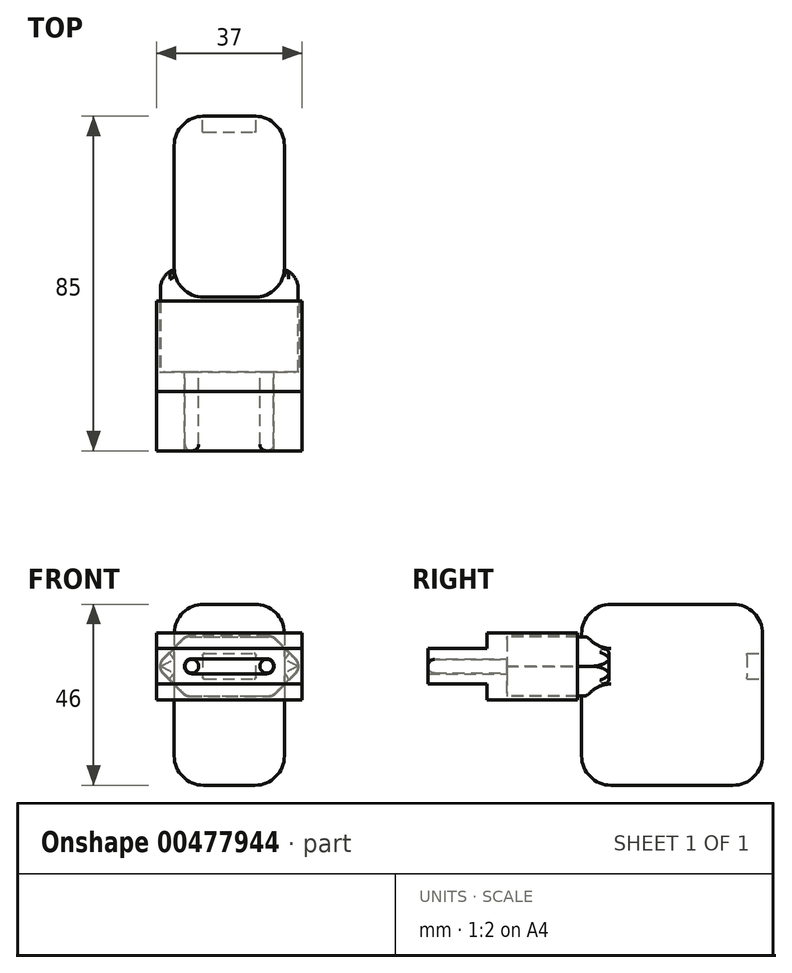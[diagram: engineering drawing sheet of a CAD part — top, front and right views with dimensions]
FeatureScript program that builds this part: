
annotation { "Feature Type Name" : "Feature", "Feature Type Description" : "" }
export const myFeature = defineFeature(function(context is Context, id is Id, definition is map)
    precondition{}
    {
        {
            var Q0;
            Q0=qCreatedBy(makeId("Front.planeOp"),FACE);
            var sketch = newSketch(context, id + "F0", { "sketchPlane" : qUnion([Q0])});
            skLineSegment(sketch, "E0.bottom", {"start": v(-14, 23) * mm, "end": v(14, 23) * mm});
            skLineSegment(sketch, "E0.top", {"start": v(-14, -23) * mm, "end": v(14, -23) * mm});
            skLineSegment(sketch, "E0.left", {"start": v(-14, 23) * mm, "end": v(-14, -23) * mm});
            skLineSegment(sketch, "E0.right", {"start": v(14, 23) * mm, "end": v(14, -23) * mm});
            skPoint(sketch, "E0.middle", {"position": v(0, 0) * mm});
            skLineSegment(sketch, "E1.bottom", {"start": v(-6.75, 10.5) * mm, "end": v(6.75, 10.5) * mm});
            skLineSegment(sketch, "E1.top", {"start": v(-6.75, 4) * mm, "end": v(6.75, 4) * mm});
            skLineSegment(sketch, "E1.left", {"start": v(-6.75, 10.5) * mm, "end": v(-6.75, 4) * mm});
            skLineSegment(sketch, "E1.right", {"start": v(6.75, 10.5) * mm, "end": v(6.75, 4) * mm});
            skPoint(sketch, "E1.middle", {"position": v(0, 7.25) * mm});
            skLineSegment(sketch, "E2.bottom", {"start": v(-17.5, 14.75) * mm, "end": v(17.5, 14.75) * mm});
            skLineSegment(sketch, "E2.top", {"start": v(-17.5, -0.25) * mm, "end": v(17.5, -0.25) * mm});
            skLineSegment(sketch, "E2.left", {"start": v(-17.5, 14.75) * mm, "end": v(-17.5, -0.25) * mm});
            skLineSegment(sketch, "E2.right", {"start": v(17.5, 14.75) * mm, "end": v(17.5, -0.25) * mm});
            skCircle(sketch, "E3", {"center": v(-9.5, 7.25) * mm, "radius": 1.75 * mm});
            skCircle(sketch, "E4", {"center": v(9.5, 7.25) * mm, "radius": 1.75 * mm});
            skSolve(sketch);
        }
        {
            var Q0;
            {var subQ0=sQuery(id+"F0.wireOp",EDGE,"E0.top");Q0=makeQuery(id+"F0.imprint","IMPRINT",FACE,{"disambiguationData":[TD([[makeQuery(id+"F0.imprint","IMPRINT",EDGE,{"derivedFrom":subQ0}),1.0]])]});}
            var Q1;
            Q1=makeQuery(id+"F0.imprint","IMPRINT",FACE,{"disambiguationData":[TD([[makeQuery(id+"F0.imprint","IMPRINT",EDGE,{"derivedFrom":sQuery(id+"F0.wireOp",EDGE,"E1.bottom")}),1.0]])]});
            var Q2;
            {var subQ0=sQuery(id+"F0.wireOp",EDGE,"E0.bottom");Q2=makeQuery(id+"F0.imprint","IMPRINT",FACE,{"disambiguationData":[TD([[makeQuery(id+"F0.imprint","IMPRINT",EDGE,{"derivedFrom":subQ0}),-1.0]])]});}
            var Q3;
            Q3=makeQuery(id+"F0.imprint","IMPRINT",FACE,{"disambiguationData":[TD([[makeQuery(id+"F0.imprint","IMPRINT",EDGE,{"derivedFrom":sQuery(id+"F0.wireOp",EDGE,"E1.bottom")}),-1.0]])]});
            var Q4;
            Q4=makeQuery(id+"F0.imprint","IMPRINT",FACE,{"disambiguationData":[TD([[makeQuery(id+"F0.imprint","IMPRINT",EDGE,{"derivedFrom":sQuery(id+"F0.wireOp",EDGE,"E3")}),1.0]])]});
            var Q5;
            Q5=makeQuery(id+"F0.imprint","IMPRINT",FACE,{"disambiguationData":[TD([[makeQuery(id+"F0.imprint","IMPRINT",EDGE,{"derivedFrom":sQuery(id+"F0.wireOp",EDGE,"E4")}),1.0]])]});
            extrude(context, id + "F1", {"entities" : qUnion([Q0, Q1, Q2, Q3, Q4, Q5]), "depth" : 46 * mm, "offsetDistance" : 25 * mm});
        }
        {
            var Q0;
            Q0=makeQuery(id+"F1.opExtrude","CAP_FACE",FACE,{"disambiguationData":[OSD([sQuery(id+"F0.wireOp",EDGE,"E0.bottom"),sQuery(id+"F0.wireOp",EDGE,"E0.top"),sQuery(id+"F0.wireOp",EDGE,"E0.left"),sQuery(id+"F0.wireOp",EDGE,"E0.right")])],"isStart":false});
            var sketch = newSketch(context, id + "F2", { "sketchPlane" : qUnion([Q0])});
            skLineSegment(sketch, "E5.0", {"start": v(-17.5, 14.75) * mm, "end": v(17.5, 14.75) * mm});
            skLineSegment(sketch, "E6.0", {"start": v(-17.5, 14.75) * mm, "end": v(-17.5, -0.25) * mm});
            skLineSegment(sketch, "E7.0", {"start": v(-17.5, -0.25) * mm, "end": v(17.5, -0.25) * mm});
            skLineSegment(sketch, "E8.0", {"start": v(17.5, 14.75) * mm, "end": v(17.5, -0.25) * mm});
            skPoint(sketch, "E9.0", {"position": v(0, 7.25) * mm});
            skCircle(sketch, "E10.0", {"center": v(-9.5, 7.25) * mm, "radius": 1.75 * mm});
            skCircle(sketch, "E10.1", {"center": v(9.5, 7.25) * mm, "radius": 1.75 * mm});
            skSolve(sketch);
        }
        {
            var Q0;
            Q0=makeQuery(id+"F2.imprint","IMPRINT",FACE,{"disambiguationData":[TD([[makeQuery(id+"F2.imprint","IMPRINT",EDGE,{"derivedFrom":sQuery(id+"F2.wireOp",EDGE,"E10.0")}),1.0]])]});
            var Q1;
            Q1=makeQuery(id+"F2.imprint","IMPRINT",FACE,{"disambiguationData":[TD([[makeQuery(id+"F2.imprint","IMPRINT",EDGE,{"derivedFrom":sQuery(id+"F2.wireOp",EDGE,"E10.1")}),1.0]])]});
            extrude(context, id + "F3", {"entities" : qUnion([Q0, Q1]), "operationType" : NewBodyOperationType.ADD, "depth" : 39 * mm, "offsetDistance" : 25 * mm});
        }
        {
            var Q0;
            {var subQ0=sQuery(id+"F2.wireOp",EDGE,"E6.0");Q0=makeQuery(id+"F2.imprint","IMPRINT",FACE,{"disambiguationData":[TD([[makeQuery(id+"F2.imprint","IMPRINT",EDGE,{"derivedFrom":subQ0}),1.0]])]});}
            var Q1;
            Q1=makeQuery(id+"F2.imprint","IMPRINT",FACE,{"disambiguationData":[TD([[makeQuery(id+"F2.imprint","IMPRINT",EDGE,{"derivedFrom":sQuery(id+"F2.wireOp",EDGE,"E10.0")}),-1.0]])]});
            var Q2;
            {var subQ0=sQuery(id+"F2.wireOp",EDGE,"E8.0");Q2=makeQuery(id+"F2.imprint","IMPRINT",FACE,{"disambiguationData":[TD([[makeQuery(id+"F2.imprint","IMPRINT",EDGE,{"derivedFrom":subQ0}),-1.0]])]});}
            extrude(context, id + "F4", {"entities" : qUnion([Q0, Q1, Q2]), "operationType" : NewBodyOperationType.ADD, "depth" : 19 * mm, "offsetDistance" : 25 * mm});
        }
        {
            var Q0;
            {var subQ0=sQuery(id+"F2.wireOp",EDGE,"E6.0");Q0=makeQuery(id+"F2.imprint","IMPRINT",FACE,{"disambiguationData":[TD([[makeQuery(id+"F2.imprint","IMPRINT",EDGE,{"derivedFrom":subQ0}),1.0]])]});}
            var Q1;
            {var subQ0=sQuery(id+"F2.wireOp",EDGE,"E8.0");Q1=makeQuery(id+"F2.imprint","IMPRINT",FACE,{"disambiguationData":[TD([[makeQuery(id+"F2.imprint","IMPRINT",EDGE,{"derivedFrom":subQ0}),-1.0]])]});}
            extrude(context, id + "F5", {"entities" : qUnion([Q0, Q1]), "operationType" : NewBodyOperationType.ADD, "oppositeDirection" : true, "depth" : 7 * mm, "offsetDistance" : 25 * mm});
        }
        {
            var Q0;
            Q0=makeQuery(id+"F3.opExtrude","CAP_EDGE",EDGE,{"disambiguationData":[OSD([sQuery(id+"F2.wireOp",EDGE,"E10.0")])],"isStart":false});
            var Q1;
            Q1=makeQuery(id+"F3.opExtrude","CAP_EDGE",EDGE,{"disambiguationData":[OSD([sQuery(id+"F2.wireOp",EDGE,"E10.1")])],"isStart":false});
            fillet(context, id + "F6", {"entities" : qUnion([Q0, Q1]), "radius" : 1.65 * mm, "tangentPropagation" : true, "allowEdgeOverflow" : false});
        }
        {
            var Q0;
            Q0=makeQuery(id+"F5.opExtrude","CAP_EDGE",EDGE,{"disambiguationData":[OSD([sQuery(id+"F2.wireOp",EDGE,"E8.0")])],"isStart":false});
            var Q1;
            Q1=makeQuery(id+"F5.opExtrude","CAP_EDGE",EDGE,{"disambiguationData":[OSD([sQuery(id+"F2.wireOp",EDGE,"E6.0")])],"isStart":false});
            var Q2;
            {var subQ0=sQuery(id+"F2.wireOp",EDGE,"E7.0");Q2=makeQuery(id+"F5.opExtrude","CAP_EDGE",EDGE,{"disambiguationData":[OSD([subQ0]),TDD([makeQuery(id+"F2.imprint","IMPRINT",EDGE,{"disambiguationData":[TD([[makeQuery(id+"F2.imprint","INTERSECT",VERTEX,{"derivedFrom":[subQ0,sQuery(id+"F2.wireOp",EDGE,"E8.0")]}),1.0]])],"derivedFrom":subQ0})])],"isStart":false});}
            var Q3;
            {var subQ0=sQuery(id+"F2.wireOp",EDGE,"E5.0");Q3=makeQuery(id+"F5.opExtrude","CAP_EDGE",EDGE,{"disambiguationData":[OSD([subQ0]),TDD([makeQuery(id+"F2.imprint","IMPRINT",EDGE,{"disambiguationData":[TD([[makeQuery(id+"F2.imprint","INTERSECT",VERTEX,{"derivedFrom":[subQ0,sQuery(id+"F2.wireOp",EDGE,"E8.0")]}),1.0]])],"derivedFrom":subQ0})])],"isStart":false});}
            var Q4;
            {var subQ0=sQuery(id+"F2.wireOp",EDGE,"E7.0");Q4=makeQuery(id+"F5.opExtrude","CAP_EDGE",EDGE,{"disambiguationData":[OSD([subQ0]),TDD([makeQuery(id+"F2.imprint","IMPRINT",EDGE,{"disambiguationData":[TD([[makeQuery(id+"F2.imprint","INTERSECT",VERTEX,{"derivedFrom":[sQuery(id+"F2.wireOp",EDGE,"E6.0"),subQ0]}),-1.0]])],"derivedFrom":subQ0})])],"isStart":false});}
            var Q5;
            {var subQ0=sQuery(id+"F2.wireOp",EDGE,"E5.0");Q5=makeQuery(id+"F5.opExtrude","CAP_EDGE",EDGE,{"disambiguationData":[OSD([subQ0]),TDD([makeQuery(id+"F2.imprint","IMPRINT",EDGE,{"disambiguationData":[TD([[makeQuery(id+"F2.imprint","INTERSECT",VERTEX,{"derivedFrom":[subQ0,sQuery(id+"F2.wireOp",EDGE,"E6.0")]}),-1.0]])],"derivedFrom":subQ0})])],"isStart":false});}
            fillet(context, id + "F7", {"entities" : qUnion([Q0, Q1, Q2, Q3, Q4, Q5]), "radius" : 5 * mm, "tangentPropagation" : true, "allowEdgeOverflow" : false});
        }
        {
            var Q0;
            {var subQ0=sQuery(id+"F2.wireOp",EDGE,"E8.0");var subQ1=sQuery(id+"F2.wireOp",EDGE,"E5.0");Q0=makeQuery(id+"F5.boolean.opBoolean","MERGE",EDGE,{"derivedFrom":[makeQuery(id+"F4.opExtrude","SWEPT_EDGE",EDGE,{"disambiguationData":[OSD([subQ1,subQ0])]}),makeQuery(id+"F5.opExtrude","SWEPT_EDGE",EDGE,{"disambiguationData":[OSD([subQ1,subQ0])]})]});}
            var Q1;
            {var subQ0=sQuery(id+"F2.wireOp",EDGE,"E8.0");var subQ1=sQuery(id+"F2.wireOp",EDGE,"E7.0");Q1=makeQuery(id+"F5.boolean.opBoolean","MERGE",EDGE,{"derivedFrom":[makeQuery(id+"F4.opExtrude","SWEPT_EDGE",EDGE,{"disambiguationData":[OSD([subQ1,subQ0])]}),makeQuery(id+"F5.opExtrude","SWEPT_EDGE",EDGE,{"disambiguationData":[OSD([subQ1,subQ0])]})]});}
            var Q2;
            {var subQ0=sQuery(id+"F2.wireOp",EDGE,"E7.0");var subQ1=sQuery(id+"F2.wireOp",EDGE,"E6.0");Q2=makeQuery(id+"F5.boolean.opBoolean","MERGE",EDGE,{"derivedFrom":[makeQuery(id+"F4.opExtrude","SWEPT_EDGE",EDGE,{"disambiguationData":[OSD([subQ1,subQ0])]}),makeQuery(id+"F5.opExtrude","SWEPT_EDGE",EDGE,{"disambiguationData":[OSD([subQ1,subQ0])]})]});}
            var Q3;
            {var subQ0=sQuery(id+"F2.wireOp",EDGE,"E6.0");var subQ1=sQuery(id+"F2.wireOp",EDGE,"E5.0");Q3=makeQuery(id+"F5.boolean.opBoolean","MERGE",EDGE,{"derivedFrom":[makeQuery(id+"F4.opExtrude","SWEPT_EDGE",EDGE,{"disambiguationData":[OSD([subQ1,subQ0])]}),makeQuery(id+"F5.opExtrude","SWEPT_EDGE",EDGE,{"disambiguationData":[OSD([subQ1,subQ0])]})]});}
            chamfer(context, id + "F8", {"entities" : qUnion([Q0, Q1, Q2, Q3]), "width" : 6.5 * mm});
        }
        {
            var Q0;
            {var subQ0=sQuery(id+"F2.wireOp",EDGE,"E8.0");var subQ1=sQuery(id+"F2.wireOp",EDGE,"E7.0");Q0=makeQuery(id+"F8.opChamfer","BLEND_EDGE",EDGE,{"blendedFrom":[makeQuery(id+"F5.boolean.opBoolean","MERGE",EDGE,{"derivedFrom":[makeQuery(id+"F4.opExtrude","SWEPT_EDGE",EDGE,{"disambiguationData":[OSD([subQ1,subQ0])]}),makeQuery(id+"F5.opExtrude","SWEPT_EDGE",EDGE,{"disambiguationData":[OSD([subQ1,subQ0])]})]}),makeQuery(id+"F5.boolean.opBoolean","MERGE",FACE,{"derivedFrom":[makeQuery(id+"F4.opExtrude","SWEPT_FACE",FACE,{"disambiguationData":[OSD([subQ1])]}),makeQuery(id+"F5.opExtrude","SWEPT_FACE",FACE,{"disambiguationData":[OSD([subQ1]),TDD([makeQuery(id+"F2.imprint","IMPRINT",EDGE,{"disambiguationData":[TD([[makeQuery(id+"F2.imprint","INTERSECT",VERTEX,{"derivedFrom":[sQuery(id+"F2.wireOp",EDGE,"E6.0"),subQ1]}),-1.0]])],"derivedFrom":subQ1})])]}),makeQuery(id+"F5.opExtrude","SWEPT_FACE",FACE,{"disambiguationData":[OSD([subQ1]),TDD([makeQuery(id+"F2.imprint","IMPRINT",EDGE,{"disambiguationData":[TD([[makeQuery(id+"F2.imprint","INTERSECT",VERTEX,{"derivedFrom":[subQ1,subQ0]}),1.0]])],"derivedFrom":subQ1})])]})]})],"blendedInto":[makeQuery(id+"F5.boolean.opBoolean","MERGE",FACE,{"derivedFrom":[makeQuery(id+"F4.opExtrude","SWEPT_FACE",FACE,{"disambiguationData":[OSD([subQ1])]}),makeQuery(id+"F5.opExtrude","SWEPT_FACE",FACE,{"disambiguationData":[OSD([subQ1]),TDD([makeQuery(id+"F2.imprint","IMPRINT",EDGE,{"disambiguationData":[TD([[makeQuery(id+"F2.imprint","INTERSECT",VERTEX,{"derivedFrom":[sQuery(id+"F2.wireOp",EDGE,"E6.0"),subQ1]}),-1.0]])],"derivedFrom":subQ1})])]}),makeQuery(id+"F5.opExtrude","SWEPT_FACE",FACE,{"disambiguationData":[OSD([subQ1]),TDD([makeQuery(id+"F2.imprint","IMPRINT",EDGE,{"disambiguationData":[TD([[makeQuery(id+"F2.imprint","INTERSECT",VERTEX,{"derivedFrom":[subQ1,subQ0]}),1.0]])],"derivedFrom":subQ1})])]})]})]});}
            var Q1;
            {var subQ0=sQuery(id+"F2.wireOp",EDGE,"E7.0");var subQ1=sQuery(id+"F2.wireOp",EDGE,"E6.0");Q1=makeQuery(id+"F8.opChamfer","BLEND_EDGE",EDGE,{"blendedFrom":[makeQuery(id+"F5.boolean.opBoolean","MERGE",EDGE,{"derivedFrom":[makeQuery(id+"F4.opExtrude","SWEPT_EDGE",EDGE,{"disambiguationData":[OSD([subQ1,subQ0])]}),makeQuery(id+"F5.opExtrude","SWEPT_EDGE",EDGE,{"disambiguationData":[OSD([subQ1,subQ0])]})]}),makeQuery(id+"F5.boolean.opBoolean","MERGE",FACE,{"derivedFrom":[makeQuery(id+"F4.opExtrude","SWEPT_FACE",FACE,{"disambiguationData":[OSD([subQ0])]}),makeQuery(id+"F5.opExtrude","SWEPT_FACE",FACE,{"disambiguationData":[OSD([subQ0]),TDD([makeQuery(id+"F2.imprint","IMPRINT",EDGE,{"disambiguationData":[TD([[makeQuery(id+"F2.imprint","INTERSECT",VERTEX,{"derivedFrom":[subQ1,subQ0]}),-1.0]])],"derivedFrom":subQ0})])]}),makeQuery(id+"F5.opExtrude","SWEPT_FACE",FACE,{"disambiguationData":[OSD([subQ0]),TDD([makeQuery(id+"F2.imprint","IMPRINT",EDGE,{"disambiguationData":[TD([[makeQuery(id+"F2.imprint","INTERSECT",VERTEX,{"derivedFrom":[subQ0,sQuery(id+"F2.wireOp",EDGE,"E8.0")]}),1.0]])],"derivedFrom":subQ0})])]})]})],"blendedInto":[makeQuery(id+"F5.boolean.opBoolean","MERGE",FACE,{"derivedFrom":[makeQuery(id+"F4.opExtrude","SWEPT_FACE",FACE,{"disambiguationData":[OSD([subQ0])]}),makeQuery(id+"F5.opExtrude","SWEPT_FACE",FACE,{"disambiguationData":[OSD([subQ0]),TDD([makeQuery(id+"F2.imprint","IMPRINT",EDGE,{"disambiguationData":[TD([[makeQuery(id+"F2.imprint","INTERSECT",VERTEX,{"derivedFrom":[subQ1,subQ0]}),-1.0]])],"derivedFrom":subQ0})])]}),makeQuery(id+"F5.opExtrude","SWEPT_FACE",FACE,{"disambiguationData":[OSD([subQ0]),TDD([makeQuery(id+"F2.imprint","IMPRINT",EDGE,{"disambiguationData":[TD([[makeQuery(id+"F2.imprint","INTERSECT",VERTEX,{"derivedFrom":[subQ0,sQuery(id+"F2.wireOp",EDGE,"E8.0")]}),1.0]])],"derivedFrom":subQ0})])]})]})]});}
            var Q2;
            {var subQ0=sQuery(id+"F2.wireOp",EDGE,"E6.0");var subQ1=sQuery(id+"F2.wireOp",EDGE,"E7.0");Q2=makeQuery(id+"F8.opChamfer","BLEND_EDGE",EDGE,{"blendedFrom":[makeQuery(id+"F5.boolean.opBoolean","MERGE",EDGE,{"derivedFrom":[makeQuery(id+"F4.opExtrude","SWEPT_EDGE",EDGE,{"disambiguationData":[OSD([subQ0,subQ1])]}),makeQuery(id+"F5.opExtrude","SWEPT_EDGE",EDGE,{"disambiguationData":[OSD([subQ0,subQ1])]})]}),makeQuery(id+"F5.boolean.opBoolean","MERGE",FACE,{"derivedFrom":[makeQuery(id+"F4.opExtrude","SWEPT_FACE",FACE,{"disambiguationData":[OSD([subQ0])]}),makeQuery(id+"F5.opExtrude","SWEPT_FACE",FACE,{"disambiguationData":[OSD([subQ0])]})]})],"blendedInto":[makeQuery(id+"F5.boolean.opBoolean","MERGE",FACE,{"derivedFrom":[makeQuery(id+"F4.opExtrude","SWEPT_FACE",FACE,{"disambiguationData":[OSD([subQ0])]}),makeQuery(id+"F5.opExtrude","SWEPT_FACE",FACE,{"disambiguationData":[OSD([subQ0])]})]})]});}
            var Q3;
            {var subQ0=sQuery(id+"F2.wireOp",EDGE,"E6.0");var subQ1=sQuery(id+"F2.wireOp",EDGE,"E5.0");Q3=makeQuery(id+"F8.opChamfer","BLEND_EDGE",EDGE,{"blendedFrom":[makeQuery(id+"F5.boolean.opBoolean","MERGE",EDGE,{"derivedFrom":[makeQuery(id+"F4.opExtrude","SWEPT_EDGE",EDGE,{"disambiguationData":[OSD([subQ1,subQ0])]}),makeQuery(id+"F5.opExtrude","SWEPT_EDGE",EDGE,{"disambiguationData":[OSD([subQ1,subQ0])]})]}),makeQuery(id+"F5.boolean.opBoolean","MERGE",FACE,{"derivedFrom":[makeQuery(id+"F4.opExtrude","SWEPT_FACE",FACE,{"disambiguationData":[OSD([subQ0])]}),makeQuery(id+"F5.opExtrude","SWEPT_FACE",FACE,{"disambiguationData":[OSD([subQ0])]})]})],"blendedInto":[makeQuery(id+"F5.boolean.opBoolean","MERGE",FACE,{"derivedFrom":[makeQuery(id+"F4.opExtrude","SWEPT_FACE",FACE,{"disambiguationData":[OSD([subQ0])]}),makeQuery(id+"F5.opExtrude","SWEPT_FACE",FACE,{"disambiguationData":[OSD([subQ0])]})]})]});}
            var Q4;
            {var subQ0=sQuery(id+"F2.wireOp",EDGE,"E5.0");var subQ1=sQuery(id+"F2.wireOp",EDGE,"E6.0");Q4=makeQuery(id+"F8.opChamfer","BLEND_EDGE",EDGE,{"blendedFrom":[makeQuery(id+"F5.boolean.opBoolean","MERGE",EDGE,{"derivedFrom":[makeQuery(id+"F4.opExtrude","SWEPT_EDGE",EDGE,{"disambiguationData":[OSD([subQ0,subQ1])]}),makeQuery(id+"F5.opExtrude","SWEPT_EDGE",EDGE,{"disambiguationData":[OSD([subQ0,subQ1])]})]}),makeQuery(id+"F5.boolean.opBoolean","MERGE",FACE,{"derivedFrom":[makeQuery(id+"F4.opExtrude","SWEPT_FACE",FACE,{"disambiguationData":[OSD([subQ0])]}),makeQuery(id+"F5.opExtrude","SWEPT_FACE",FACE,{"disambiguationData":[OSD([subQ0]),TDD([makeQuery(id+"F2.imprint","IMPRINT",EDGE,{"disambiguationData":[TD([[makeQuery(id+"F2.imprint","INTERSECT",VERTEX,{"derivedFrom":[subQ0,subQ1]}),-1.0]])],"derivedFrom":subQ0})])]}),makeQuery(id+"F5.opExtrude","SWEPT_FACE",FACE,{"disambiguationData":[OSD([subQ0]),TDD([makeQuery(id+"F2.imprint","IMPRINT",EDGE,{"disambiguationData":[TD([[makeQuery(id+"F2.imprint","INTERSECT",VERTEX,{"derivedFrom":[subQ0,sQuery(id+"F2.wireOp",EDGE,"E8.0")]}),1.0]])],"derivedFrom":subQ0})])]})]})],"blendedInto":[makeQuery(id+"F5.boolean.opBoolean","MERGE",FACE,{"derivedFrom":[makeQuery(id+"F4.opExtrude","SWEPT_FACE",FACE,{"disambiguationData":[OSD([subQ0])]}),makeQuery(id+"F5.opExtrude","SWEPT_FACE",FACE,{"disambiguationData":[OSD([subQ0]),TDD([makeQuery(id+"F2.imprint","IMPRINT",EDGE,{"disambiguationData":[TD([[makeQuery(id+"F2.imprint","INTERSECT",VERTEX,{"derivedFrom":[subQ0,subQ1]}),-1.0]])],"derivedFrom":subQ0})])]}),makeQuery(id+"F5.opExtrude","SWEPT_FACE",FACE,{"disambiguationData":[OSD([subQ0]),TDD([makeQuery(id+"F2.imprint","IMPRINT",EDGE,{"disambiguationData":[TD([[makeQuery(id+"F2.imprint","INTERSECT",VERTEX,{"derivedFrom":[subQ0,sQuery(id+"F2.wireOp",EDGE,"E8.0")]}),1.0]])],"derivedFrom":subQ0})])]})]})]});}
            var Q5;
            {var subQ0=sQuery(id+"F2.wireOp",EDGE,"E8.0");var subQ1=sQuery(id+"F2.wireOp",EDGE,"E5.0");Q5=makeQuery(id+"F8.opChamfer","BLEND_EDGE",EDGE,{"blendedFrom":[makeQuery(id+"F5.boolean.opBoolean","MERGE",EDGE,{"derivedFrom":[makeQuery(id+"F4.opExtrude","SWEPT_EDGE",EDGE,{"disambiguationData":[OSD([subQ1,subQ0])]}),makeQuery(id+"F5.opExtrude","SWEPT_EDGE",EDGE,{"disambiguationData":[OSD([subQ1,subQ0])]})]}),makeQuery(id+"F5.boolean.opBoolean","MERGE",FACE,{"derivedFrom":[makeQuery(id+"F4.opExtrude","SWEPT_FACE",FACE,{"disambiguationData":[OSD([subQ1])]}),makeQuery(id+"F5.opExtrude","SWEPT_FACE",FACE,{"disambiguationData":[OSD([subQ1]),TDD([makeQuery(id+"F2.imprint","IMPRINT",EDGE,{"disambiguationData":[TD([[makeQuery(id+"F2.imprint","INTERSECT",VERTEX,{"derivedFrom":[subQ1,sQuery(id+"F2.wireOp",EDGE,"E6.0")]}),-1.0]])],"derivedFrom":subQ1})])]}),makeQuery(id+"F5.opExtrude","SWEPT_FACE",FACE,{"disambiguationData":[OSD([subQ1]),TDD([makeQuery(id+"F2.imprint","IMPRINT",EDGE,{"disambiguationData":[TD([[makeQuery(id+"F2.imprint","INTERSECT",VERTEX,{"derivedFrom":[subQ1,subQ0]}),1.0]])],"derivedFrom":subQ1})])]})]})],"blendedInto":[makeQuery(id+"F5.boolean.opBoolean","MERGE",FACE,{"derivedFrom":[makeQuery(id+"F4.opExtrude","SWEPT_FACE",FACE,{"disambiguationData":[OSD([subQ1])]}),makeQuery(id+"F5.opExtrude","SWEPT_FACE",FACE,{"disambiguationData":[OSD([subQ1]),TDD([makeQuery(id+"F2.imprint","IMPRINT",EDGE,{"disambiguationData":[TD([[makeQuery(id+"F2.imprint","INTERSECT",VERTEX,{"derivedFrom":[subQ1,sQuery(id+"F2.wireOp",EDGE,"E6.0")]}),-1.0]])],"derivedFrom":subQ1})])]}),makeQuery(id+"F5.opExtrude","SWEPT_FACE",FACE,{"disambiguationData":[OSD([subQ1]),TDD([makeQuery(id+"F2.imprint","IMPRINT",EDGE,{"disambiguationData":[TD([[makeQuery(id+"F2.imprint","INTERSECT",VERTEX,{"derivedFrom":[subQ1,subQ0]}),1.0]])],"derivedFrom":subQ1})])]})]})]});}
            var Q6;
            {var subQ0=sQuery(id+"F2.wireOp",EDGE,"E8.0");var subQ1=sQuery(id+"F2.wireOp",EDGE,"E5.0");Q6=makeQuery(id+"F8.opChamfer","BLEND_EDGE",EDGE,{"blendedFrom":[makeQuery(id+"F5.boolean.opBoolean","MERGE",EDGE,{"derivedFrom":[makeQuery(id+"F4.opExtrude","SWEPT_EDGE",EDGE,{"disambiguationData":[OSD([subQ1,subQ0])]}),makeQuery(id+"F5.opExtrude","SWEPT_EDGE",EDGE,{"disambiguationData":[OSD([subQ1,subQ0])]})]}),makeQuery(id+"F5.boolean.opBoolean","MERGE",FACE,{"derivedFrom":[makeQuery(id+"F4.opExtrude","SWEPT_FACE",FACE,{"disambiguationData":[OSD([subQ0])]}),makeQuery(id+"F5.opExtrude","SWEPT_FACE",FACE,{"disambiguationData":[OSD([subQ0])]})]})],"blendedInto":[makeQuery(id+"F5.boolean.opBoolean","MERGE",FACE,{"derivedFrom":[makeQuery(id+"F4.opExtrude","SWEPT_FACE",FACE,{"disambiguationData":[OSD([subQ0])]}),makeQuery(id+"F5.opExtrude","SWEPT_FACE",FACE,{"disambiguationData":[OSD([subQ0])]})]})]});}
            var Q7;
            {var subQ0=sQuery(id+"F2.wireOp",EDGE,"E8.0");var subQ1=sQuery(id+"F2.wireOp",EDGE,"E7.0");Q7=makeQuery(id+"F8.opChamfer","BLEND_EDGE",EDGE,{"blendedFrom":[makeQuery(id+"F5.boolean.opBoolean","MERGE",EDGE,{"derivedFrom":[makeQuery(id+"F4.opExtrude","SWEPT_EDGE",EDGE,{"disambiguationData":[OSD([subQ1,subQ0])]}),makeQuery(id+"F5.opExtrude","SWEPT_EDGE",EDGE,{"disambiguationData":[OSD([subQ1,subQ0])]})]}),makeQuery(id+"F5.boolean.opBoolean","MERGE",FACE,{"derivedFrom":[makeQuery(id+"F4.opExtrude","SWEPT_FACE",FACE,{"disambiguationData":[OSD([subQ0])]}),makeQuery(id+"F5.opExtrude","SWEPT_FACE",FACE,{"disambiguationData":[OSD([subQ0])]})]})],"blendedInto":[makeQuery(id+"F5.boolean.opBoolean","MERGE",FACE,{"derivedFrom":[makeQuery(id+"F4.opExtrude","SWEPT_FACE",FACE,{"disambiguationData":[OSD([subQ0])]}),makeQuery(id+"F5.opExtrude","SWEPT_FACE",FACE,{"disambiguationData":[OSD([subQ0])]})]})]});}
            fillet(context, id + "F9", {"entities" : qUnion([Q0, Q1, Q2, Q3, Q4, Q5, Q6, Q7]), "radius" : 2.5 * mm, "tangentPropagation" : true, "allowEdgeOverflow" : false});
        }
        {
            var Q0;
            Q0=makeQuery(id+"F0.imprint","IMPRINT",FACE,{"disambiguationData":[TD([[makeQuery(id+"F0.imprint","IMPRINT",EDGE,{"derivedFrom":sQuery(id+"F0.wireOp",EDGE,"E1.bottom")}),-1.0]])]});
            extrude(context, id + "F10", {"entities" : qUnion([Q0]), "operationType" : NewBodyOperationType.REMOVE, "depth" : 4 * mm, "offsetDistance" : 25 * mm});
        }
        {
            var Q0;
            Q0=makeQuery(id+"F10.boolean.opBoolean","COPY",EDGE,{"derivedFrom":makeQuery(id+"F10.opExtrude","SWEPT_EDGE",EDGE,{"disambiguationData":[OSD([sQuery(id+"F0.wireOp",EDGE,"E1.bottom"),sQuery(id+"F0.wireOp",EDGE,"E1.left")])]})});
            var Q1;
            Q1=makeQuery(id+"F10.boolean.opBoolean","COPY",EDGE,{"derivedFrom":makeQuery(id+"F10.opExtrude","SWEPT_EDGE",EDGE,{"disambiguationData":[OSD([sQuery(id+"F0.wireOp",EDGE,"E1.top"),sQuery(id+"F0.wireOp",EDGE,"E1.left")])]})});
            var Q2;
            Q2=makeQuery(id+"F10.boolean.opBoolean","COPY",EDGE,{"derivedFrom":makeQuery(id+"F10.opExtrude","SWEPT_EDGE",EDGE,{"disambiguationData":[OSD([sQuery(id+"F0.wireOp",EDGE,"E1.top"),sQuery(id+"F0.wireOp",EDGE,"E1.right")])]})});
            var Q3;
            Q3=makeQuery(id+"F10.boolean.opBoolean","COPY",EDGE,{"derivedFrom":makeQuery(id+"F10.opExtrude","SWEPT_EDGE",EDGE,{"disambiguationData":[OSD([sQuery(id+"F0.wireOp",EDGE,"E1.bottom"),sQuery(id+"F0.wireOp",EDGE,"E1.right")])]})});
            fillet(context, id + "F11", {"entities" : qUnion([Q0, Q1, Q2, Q3]), "radius" : 0.5 * mm, "tangentPropagation" : true, "allowEdgeOverflow" : false});
        }
        {
            var Q0;
            Q0=makeQuery(id+"F1.opExtrude","SWEPT_EDGE",EDGE,{"disambiguationData":[OSD([sQuery(id+"F0.wireOp",EDGE,"E0.bottom"),sQuery(id+"F0.wireOp",EDGE,"E0.right")])]});
            var Q1;
            Q1=makeQuery(id+"F1.opExtrude","SWEPT_EDGE",EDGE,{"disambiguationData":[OSD([sQuery(id+"F0.wireOp",EDGE,"E0.bottom"),sQuery(id+"F0.wireOp",EDGE,"E0.left")])]});
            var Q2;
            Q2=makeQuery(id+"F1.opExtrude","SWEPT_EDGE",EDGE,{"disambiguationData":[OSD([sQuery(id+"F0.wireOp",EDGE,"E0.top"),sQuery(id+"F0.wireOp",EDGE,"E0.right")])]});
            var Q3;
            {var subQ0=sQuery(id+"F0.wireOp",EDGE,"E0.right");var subQ1=sQuery(id+"F0.wireOp",EDGE,"E0.bottom");var subQ2=makeQuery(id+"F1.opExtrude","CAP_FACE",FACE,{"disambiguationData":[OSD([subQ1,sQuery(id+"F0.wireOp",EDGE,"E0.top"),sQuery(id+"F0.wireOp",EDGE,"E0.left"),subQ0])],"isStart":false});var subQ4=makeQuery(id+"F1.opExtrude","SWEPT_FACE",FACE,{"disambiguationData":[OSD([subQ0])]});Q3=makeQuery(id+"F4.boolean.opBoolean","SPLIT",EDGE,{"disambiguationData":[topologyDisambiguationEdgeConnected([subQ2,subQ4]),TD([makeQuery(id+"F1.opExtrude","SWEPT_FACE",FACE,{"disambiguationData":[OSD([subQ1])]})])],"derivedFrom":makeQuery(id+"F1.opExtrude","CAP_EDGE",EDGE,{"disambiguationData":[OSD([subQ0])],"isStart":false})});}
            var Q4;
            {var subQ1=sQuery(id+"F0.wireOp",EDGE,"E0.right");var subQ2=makeQuery(id+"F1.opExtrude","SWEPT_FACE",FACE,{"disambiguationData":[OSD([subQ1])]});var subQ3=sQuery(id+"F0.wireOp",EDGE,"E0.top");var subQ4=makeQuery(id+"F1.opExtrude","CAP_FACE",FACE,{"disambiguationData":[OSD([sQuery(id+"F0.wireOp",EDGE,"E0.bottom"),subQ3,sQuery(id+"F0.wireOp",EDGE,"E0.left"),subQ1])],"isStart":false});Q4=makeQuery(id+"F4.boolean.opBoolean","SPLIT",EDGE,{"disambiguationData":[topologyDisambiguationEdgeConnected([subQ4,subQ2]),TD([makeQuery(id+"F1.opExtrude","SWEPT_FACE",FACE,{"disambiguationData":[OSD([subQ3])]})])],"derivedFrom":makeQuery(id+"F1.opExtrude","CAP_EDGE",EDGE,{"disambiguationData":[OSD([subQ1])],"isStart":false})});}
            var Q5;
            Q5=makeQuery(id+"F1.opExtrude","CAP_EDGE",EDGE,{"disambiguationData":[OSD([sQuery(id+"F0.wireOp",EDGE,"E0.bottom")])],"isStart":false});
            var Q6;
            Q6=makeQuery(id+"F1.opExtrude","CAP_EDGE",EDGE,{"disambiguationData":[OSD([sQuery(id+"F0.wireOp",EDGE,"E0.top")])],"isStart":false});
            var Q7;
            {var subQ0=sQuery(id+"F0.wireOp",EDGE,"E0.left");var subQ1=makeQuery(id+"F1.opExtrude","SWEPT_FACE",FACE,{"disambiguationData":[OSD([subQ0])]});var subQ2=sQuery(id+"F0.wireOp",EDGE,"E0.bottom");var subQ3=makeQuery(id+"F1.opExtrude","CAP_FACE",FACE,{"disambiguationData":[OSD([subQ2,sQuery(id+"F0.wireOp",EDGE,"E0.top"),subQ0,sQuery(id+"F0.wireOp",EDGE,"E0.right")])],"isStart":false});Q7=makeQuery(id+"F4.boolean.opBoolean","SPLIT",EDGE,{"disambiguationData":[topologyDisambiguationEdgeConnected([subQ3,subQ1]),TD([makeQuery(id+"F1.opExtrude","SWEPT_FACE",FACE,{"disambiguationData":[OSD([subQ2])]})])],"derivedFrom":makeQuery(id+"F1.opExtrude","CAP_EDGE",EDGE,{"disambiguationData":[OSD([subQ0])],"isStart":false})});}
            var Q8;
            {var subQ1=sQuery(id+"F0.wireOp",EDGE,"E0.left");var subQ2=makeQuery(id+"F1.opExtrude","SWEPT_FACE",FACE,{"disambiguationData":[OSD([subQ1])]});var subQ3=sQuery(id+"F0.wireOp",EDGE,"E0.top");var subQ4=makeQuery(id+"F1.opExtrude","CAP_FACE",FACE,{"disambiguationData":[OSD([sQuery(id+"F0.wireOp",EDGE,"E0.bottom"),subQ3,subQ1,sQuery(id+"F0.wireOp",EDGE,"E0.right")])],"isStart":false});Q8=makeQuery(id+"F4.boolean.opBoolean","SPLIT",EDGE,{"disambiguationData":[topologyDisambiguationEdgeConnected([subQ4,subQ2]),TD([makeQuery(id+"F1.opExtrude","SWEPT_FACE",FACE,{"disambiguationData":[OSD([subQ3])]})])],"derivedFrom":makeQuery(id+"F1.opExtrude","CAP_EDGE",EDGE,{"disambiguationData":[OSD([subQ1])],"isStart":false})});}
            var Q9;
            Q9=makeQuery(id+"F1.opExtrude","SWEPT_EDGE",EDGE,{"disambiguationData":[OSD([sQuery(id+"F0.wireOp",EDGE,"E0.top"),sQuery(id+"F0.wireOp",EDGE,"E0.left")])]});
            var Q10;
            Q10=makeQuery(id+"F1.opExtrude","CAP_EDGE",EDGE,{"disambiguationData":[OSD([sQuery(id+"F0.wireOp",EDGE,"E0.left")])],"isStart":true});
            var Q11;
            Q11=makeQuery(id+"F1.opExtrude","CAP_EDGE",EDGE,{"disambiguationData":[OSD([sQuery(id+"F0.wireOp",EDGE,"E0.right")])],"isStart":true});
            var Q12;
            Q12=makeQuery(id+"F1.opExtrude","CAP_EDGE",EDGE,{"disambiguationData":[OSD([sQuery(id+"F0.wireOp",EDGE,"E0.bottom")])],"isStart":true});
            var Q13;
            Q13=makeQuery(id+"F1.opExtrude","CAP_EDGE",EDGE,{"disambiguationData":[OSD([sQuery(id+"F0.wireOp",EDGE,"E0.top")])],"isStart":true});
            fillet(context, id + "F12", {"entities" : qUnion([Q0, Q1, Q2, Q3, Q4, Q5, Q6, Q7, Q8, Q9, Q10, Q11, Q12, Q13]), "radius" : 7.5 * mm, "tangentPropagation" : true, "allowEdgeOverflow" : false});
        }
        {
            var Q0;
            Q0=makeQuery(id+"F4.opExtrude","CAP_FACE",FACE,{"disambiguationData":[OSD([sQuery(id+"F2.wireOp",EDGE,"E5.0"),sQuery(id+"F2.wireOp",EDGE,"E6.0"),sQuery(id+"F2.wireOp",EDGE,"E7.0"),sQuery(id+"F2.wireOp",EDGE,"E8.0"),sQuery(id+"F2.wireOp",EDGE,"E10.0"),sQuery(id+"F2.wireOp",EDGE,"E10.1")])],"isStart":false});
            var sketch = newSketch(context, id + "F13", { "sketchPlane" : qUnion([Q0])});
            skLineSegment(sketch, "E11.0.0", {"start": v(11.73, 0.48) * mm, "end": v(16.77, 5.52) * mm});
            skArc(sketch, "E11.0.1", {"start": v(16.77, 5.52) * mm, "mid": v(17.3, 6.31) * mm, "end": v(17.5, 7.25) * mm});
            skArc(sketch, "E11.0.2", {"start": v(17.5, 7.25) * mm, "mid": v(17.3, 8.19) * mm, "end": v(16.77, 8.98) * mm});
            skLineSegment(sketch, "E11.0.3", {"start": v(16.77, 8.98) * mm, "end": v(11.73, 14.02) * mm});
            skArc(sketch, "E11.0.4", {"start": v(11.73, 14.02) * mm, "mid": v(10.92, 14.56) * mm, "end": v(9.96, 14.75) * mm});
            skLineSegment(sketch, "E11.0.5", {"start": v(9.96, 14.75) * mm, "end": v(-9.96, 14.75) * mm});
            skArc(sketch, "E11.0.6", {"start": v(-9.96, 14.75) * mm, "mid": v(-10.92, 14.56) * mm, "end": v(-11.73, 14.02) * mm});
            skLineSegment(sketch, "E11.0.7", {"start": v(-11.73, 14.02) * mm, "end": v(-16.77, 8.98) * mm});
            skArc(sketch, "E11.0.8", {"start": v(-16.77, 8.98) * mm, "mid": v(-17.3, 8.19) * mm, "end": v(-17.5, 7.25) * mm});
            skArc(sketch, "E11.0.9", {"start": v(-17.5, 7.25) * mm, "mid": v(-17.3, 6.31) * mm, "end": v(-16.77, 5.52) * mm});
            skLineSegment(sketch, "E11.0.10", {"start": v(-16.77, 5.52) * mm, "end": v(-11.73, 0.48) * mm});
            skArc(sketch, "E11.0.11", {"start": v(-11.73, 0.48) * mm, "mid": v(-10.92, -0.06) * mm, "end": v(-9.96, -0.25) * mm});
            skLineSegment(sketch, "E11.0.12", {"start": v(-9.96, -0.25) * mm, "end": v(9.96, -0.25) * mm});
            skArc(sketch, "E11.0.13", {"start": v(9.96, -0.25) * mm, "mid": v(10.92, -0.06) * mm, "end": v(11.73, 0.48) * mm});
            skCircle(sketch, "E12.0", {"center": v(-9.5, 7.25) * mm, "radius": 1.75 * mm});
            skCircle(sketch, "E13.0", {"center": v(9.5, 7.25) * mm, "radius": 1.75 * mm});
            skPoint(sketch, "E14.0", {"position": v(0, 7.25) * mm});
            skLineSegment(sketch, "E15.bottom", {"start": v(-18.5, 15.75) * mm, "end": v(18.5, 15.75) * mm});
            skLineSegment(sketch, "E15.top", {"start": v(-18.5, -1.25) * mm, "end": v(18.5, -1.25) * mm});
            skLineSegment(sketch, "E15.left", {"start": v(-18.5, 15.75) * mm, "end": v(-18.5, -1.25) * mm});
            skLineSegment(sketch, "E15.right", {"start": v(18.5, 15.75) * mm, "end": v(18.5, -1.25) * mm});
            skCircle(sketch, "E16.0", {"center": v(-9.5, 7.25) * mm, "radius": 1.9 * mm});
            skCircle(sketch, "E17.0", {"center": v(9.5, 7.25) * mm, "radius": 1.9 * mm});
            skArc(sketch, "E18.0", {"start": v(11.87, 14.16) * mm, "mid": v(11, 14.74) * mm, "end": v(9.96, 14.95) * mm});
            skLineSegment(sketch, "E18.1", {"start": v(16.9, 9.12) * mm, "end": v(11.87, 14.16) * mm});
            skArc(sketch, "E18.2", {"start": v(17.7, 7.25) * mm, "mid": v(17.49, 8.26) * mm, "end": v(16.9, 9.12) * mm});
            skArc(sketch, "E18.3", {"start": v(-17.7, 7.25) * mm, "mid": v(-17.49, 6.24) * mm, "end": v(-16.9, 5.38) * mm});
            skArc(sketch, "E18.4", {"start": v(-16.9, 9.12) * mm, "mid": v(-17.49, 8.26) * mm, "end": v(-17.7, 7.25) * mm});
            skLineSegment(sketch, "E18.5", {"start": v(-11.87, 14.16) * mm, "end": v(-16.9, 9.12) * mm});
            skArc(sketch, "E18.6", {"start": v(-9.96, 14.95) * mm, "mid": v(-11, 14.74) * mm, "end": v(-11.87, 14.16) * mm});
            skLineSegment(sketch, "E18.7", {"start": v(-16.9, 5.38) * mm, "end": v(-11.87, 0.34) * mm});
            skArc(sketch, "E18.8", {"start": v(-11.87, 0.34) * mm, "mid": v(-11, -0.24) * mm, "end": v(-9.96, -0.45) * mm});
            skLineSegment(sketch, "E18.9", {"start": v(-9.96, -0.45) * mm, "end": v(9.96, -0.45) * mm});
            skLineSegment(sketch, "E18.10", {"start": v(9.96, 14.95) * mm, "end": v(-9.96, 14.95) * mm});
            skArc(sketch, "E18.11", {"start": v(9.96, -0.45) * mm, "mid": v(11, -0.24) * mm, "end": v(11.87, 0.34) * mm});
            skLineSegment(sketch, "E18.12", {"start": v(11.87, 0.34) * mm, "end": v(16.9, 5.38) * mm});
            skArc(sketch, "E18.13", {"start": v(16.9, 5.38) * mm, "mid": v(17.49, 6.24) * mm, "end": v(17.7, 7.25) * mm});
            skLineSegment(sketch, "E19", {"start": v(-9.5, 9.15) * mm, "end": v(9.5, 9.15) * mm});
            skLineSegment(sketch, "E20", {"start": v(9.5, 5.35) * mm, "end": v(-9.5, 5.35) * mm});
            skLineSegment(sketch, "E21.bottom", {"start": v(-18.5, 11.75) * mm, "end": v(18.5, 11.75) * mm});
            skLineSegment(sketch, "E21.top", {"start": v(-18.5, 2.75) * mm, "end": v(18.5, 2.75) * mm});
            skLineSegment(sketch, "E21.left", {"start": v(-18.5, 11.75) * mm, "end": v(-18.5, 2.75) * mm});
            skLineSegment(sketch, "E21.right", {"start": v(18.5, 11.75) * mm, "end": v(18.5, 2.75) * mm});
            skSolve(sketch);
        }
        {
            var Q0;
            Q0=makeQuery(id+"F13.imprint","IMPRINT",FACE,{"disambiguationData":[TD([[makeQuery(id+"F13.imprint","IMPRINT",EDGE,{"derivedFrom":sQuery(id+"F13.wireOp",EDGE,"E15.bottom")}),-1.0]])]});
            var Q1;
            {var subQ5=sQuery(id+"F13.wireOp",EDGE,"E18.3");Q1=makeQuery(id+"F13.imprint","IMPRINT",FACE,{"disambiguationData":[TD([[makeQuery(id+"F13.imprint","IMPRINT",EDGE,{"derivedFrom":subQ5}),-1.0]])]});}
            var Q2;
            {var subQ5=sQuery(id+"F13.wireOp",EDGE,"E15.top");Q2=makeQuery(id+"F13.imprint","IMPRINT",FACE,{"disambiguationData":[TD([[makeQuery(id+"F13.imprint","IMPRINT",EDGE,{"derivedFrom":subQ5}),1.0]])]});}
            var Q3;
            {var subQ1=sQuery(id+"F13.wireOp",EDGE,"E18.2");Q3=makeQuery(id+"F13.imprint","IMPRINT",FACE,{"disambiguationData":[TD([[makeQuery(id+"F13.imprint","IMPRINT",EDGE,{"derivedFrom":subQ1}),-1.0]])]});}
            extrude(context, id + "F14", {"entities" : qUnion([Q0, Q1, Q2, Q3]), "oppositeDirection" : true, "depth" : 18 * mm, "offsetDistance" : 25 * mm});
        }
        {
            var Q0;
            Q0=makeQuery(id+"F13.imprint","IMPRINT",FACE,{"disambiguationData":[TD([[makeQuery(id+"F13.imprint","IMPRINT",EDGE,{"derivedFrom":sQuery(id+"F13.wireOp",EDGE,"E15.bottom")}),-1.0]])]});
            var Q1;
            Q1=makeQuery(id+"F13.imprint","IMPRINT",FACE,{"disambiguationData":[TD([[makeQuery(id+"F13.imprint","IMPRINT",EDGE,{"derivedFrom":sQuery(id+"F13.wireOp",EDGE,"E11.0.0")}),1.0]])]});
            var Q2;
            {var subQ1=sQuery(id+"F13.wireOp",EDGE,"E18.2");Q2=makeQuery(id+"F13.imprint","IMPRINT",FACE,{"disambiguationData":[TD([[makeQuery(id+"F13.imprint","IMPRINT",EDGE,{"derivedFrom":subQ1}),-1.0]])]});}
            var Q3;
            {var subQ5=sQuery(id+"F13.wireOp",EDGE,"E15.top");Q3=makeQuery(id+"F13.imprint","IMPRINT",FACE,{"disambiguationData":[TD([[makeQuery(id+"F13.imprint","IMPRINT",EDGE,{"derivedFrom":subQ5}),1.0]])]});}
            var Q4;
            {var subQ5=sQuery(id+"F13.wireOp",EDGE,"E18.3");Q4=makeQuery(id+"F13.imprint","IMPRINT",FACE,{"disambiguationData":[TD([[makeQuery(id+"F13.imprint","IMPRINT",EDGE,{"derivedFrom":subQ5}),-1.0]])]});}
            var Q5;
            {var subQ16=sQuery(id+"F13.wireOp",EDGE,"E11.0.1");Q5=makeQuery(id+"F13.imprint","IMPRINT",FACE,{"disambiguationData":[TD([[makeQuery(id+"F13.imprint","IMPRINT",EDGE,{"derivedFrom":subQ16}),1.0]])]});}
            var Q6;
            {var subQ6=sQuery(id+"F13.wireOp",EDGE,"E11.0.4");Q6=makeQuery(id+"F13.imprint","IMPRINT",FACE,{"disambiguationData":[TD([[makeQuery(id+"F13.imprint","IMPRINT",EDGE,{"derivedFrom":subQ6}),1.0]])]});}
            var Q7;
            {var subQ10=sQuery(id+"F13.wireOp",EDGE,"E11.0.4");Q7=makeQuery(id+"F13.imprint","IMPRINT",FACE,{"disambiguationData":[TD([[makeQuery(id+"F13.imprint","IMPRINT",EDGE,{"derivedFrom":subQ10}),-1.0]])]});}
            var Q8;
            {var subQ10=sQuery(id+"F13.wireOp",EDGE,"E11.0.1");Q8=makeQuery(id+"F13.imprint","IMPRINT",FACE,{"disambiguationData":[TD([[makeQuery(id+"F13.imprint","IMPRINT",EDGE,{"derivedFrom":subQ10}),-1.0]])]});}
            var Q9;
            {var subQ10=sQuery(id+"F13.wireOp",EDGE,"E11.0.11");Q9=makeQuery(id+"F13.imprint","IMPRINT",FACE,{"disambiguationData":[TD([[makeQuery(id+"F13.imprint","IMPRINT",EDGE,{"derivedFrom":subQ10}),-1.0]])]});}
            var Q10;
            {var subQ7=sQuery(id+"F13.wireOp",EDGE,"E11.0.8");Q10=makeQuery(id+"F13.imprint","IMPRINT",FACE,{"disambiguationData":[TD([[makeQuery(id+"F13.imprint","IMPRINT",EDGE,{"derivedFrom":subQ7}),-1.0]])]});}
            extrude(context, id + "F15", {"entities" : qUnion([Q0, Q1, Q2, Q3, Q4, Q5, Q6, Q7, Q8, Q9, Q10]), "operationType" : NewBodyOperationType.ADD, "depth" : 5 * mm, "offsetDistance" : 25 * mm});
        }
        {
            var Q0;
            {var subQ5=sQuery(id+"F13.wireOp",EDGE,"E18.3");Q0=makeQuery(id+"F13.imprint","IMPRINT",FACE,{"disambiguationData":[TD([[makeQuery(id+"F13.imprint","IMPRINT",EDGE,{"derivedFrom":subQ5}),-1.0]])]});}
            var Q1;
            {var subQ7=sQuery(id+"F13.wireOp",EDGE,"E11.0.8");Q1=makeQuery(id+"F13.imprint","IMPRINT",FACE,{"disambiguationData":[TD([[makeQuery(id+"F13.imprint","IMPRINT",EDGE,{"derivedFrom":subQ7}),-1.0]])]});}
            var Q2;
            {var subQ16=sQuery(id+"F13.wireOp",EDGE,"E11.0.1");Q2=makeQuery(id+"F13.imprint","IMPRINT",FACE,{"disambiguationData":[TD([[makeQuery(id+"F13.imprint","IMPRINT",EDGE,{"derivedFrom":subQ16}),1.0]])]});}
            var Q3;
            {var subQ10=sQuery(id+"F13.wireOp",EDGE,"E11.0.1");Q3=makeQuery(id+"F13.imprint","IMPRINT",FACE,{"disambiguationData":[TD([[makeQuery(id+"F13.imprint","IMPRINT",EDGE,{"derivedFrom":subQ10}),-1.0]])]});}
            var Q4;
            {var subQ1=sQuery(id+"F13.wireOp",EDGE,"E18.2");Q4=makeQuery(id+"F13.imprint","IMPRINT",FACE,{"disambiguationData":[TD([[makeQuery(id+"F13.imprint","IMPRINT",EDGE,{"derivedFrom":subQ1}),-1.0]])]});}
            extrude(context, id + "F16", {"entities" : qUnion([Q0, Q1, Q2, Q3, Q4]), "operationType" : NewBodyOperationType.ADD, "depth" : 20 * mm, "offsetDistance" : 25 * mm});
        }
    });
